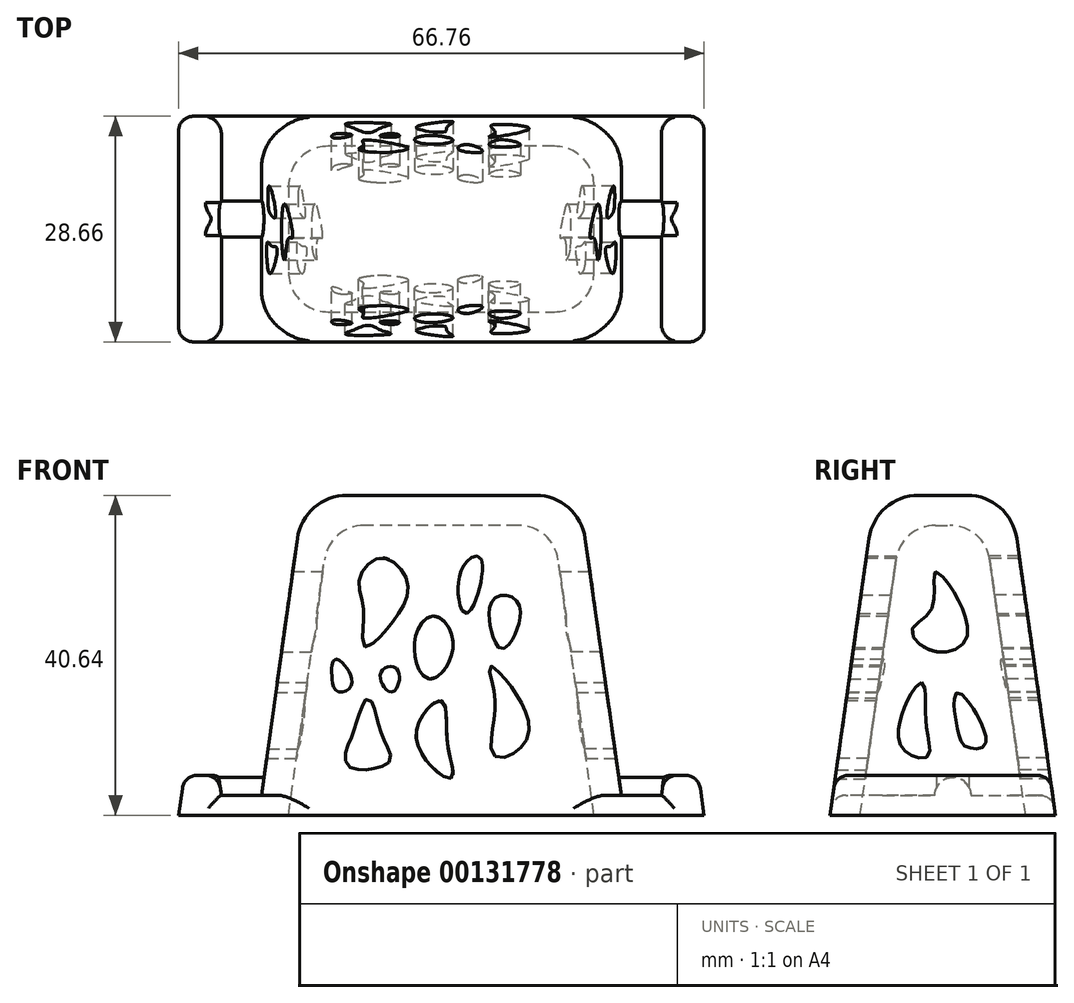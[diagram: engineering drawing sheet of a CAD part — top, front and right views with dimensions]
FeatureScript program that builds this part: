
annotation { "Feature Type Name" : "Feature", "Feature Type Description" : "" }
export const myFeature = defineFeature(function(context is Context, id is Id, definition is map)
    precondition{}
    {
        {
            var Q0;
            Q0=qCreatedBy(makeId("Top.planeOp"),FACE);
            cPlane(context, id + "F0", {"entities" : qUnion([Q0]), "cplaneType" : CPlaneType.OFFSET, "offset" : 38.1 * mm, "oppositeDirection" : true, "width" : 152.4 * mm, "height" : 152.4 * mm});
        }
        {
            var Q0;
            Q0=qCreatedBy(id+"F0.planeOp",FACE);
            var sketch = newSketch(context, id + "F1", { "sketchPlane" : qUnion([Q0])});
            skLineSegment(sketch, "E0.bottom", {"start": v(22.86, -13.97) * mm, "end": v(-22.86, -13.97) * mm});
            skLineSegment(sketch, "E0.top", {"start": v(22.86, 13.97) * mm, "end": v(-22.86, 13.97) * mm});
            skLineSegment(sketch, "E0.left", {"start": v(22.86, -13.97) * mm, "end": v(22.86, 13.97) * mm});
            skLineSegment(sketch, "E0.right", {"start": v(-22.86, -13.97) * mm, "end": v(-22.86, 13.97) * mm});
            skPoint(sketch, "E0.middle", {"position": v(0, 0) * mm});
            skLineSegment(sketch, "E1", {"start": v(22.86, 13.97) * mm, "end": v(33.02, 13.97) * mm});
            skLineSegment(sketch, "E2", {"start": v(33.02, 13.97) * mm, "end": v(33.02, -13.97) * mm});
            skLineSegment(sketch, "E3", {"start": v(33.02, -13.97) * mm, "end": v(22.86, -13.97) * mm});
            skLineSegment(sketch, "E4", {"start": v(0, -33.3) * mm, "end": v(0, 38) * mm, "construction": true});
            skPoint(sketch, "E4.endSnap0", {"position": v(0, 13.97) * mm});
            skLineSegment(sketch, "E5.MirrorCS", {"start": v(-33.02, -13.97) * mm, "end": v(-22.86, -13.97) * mm});
            skLineSegment(sketch, "E6.MirrorCS", {"start": v(-22.86, 13.97) * mm, "end": v(-33.02, 13.97) * mm});
            skLineSegment(sketch, "E7.MirrorCS", {"start": v(-33.02, 13.97) * mm, "end": v(-33.02, -13.97) * mm});
            skLineSegment(sketch, "E8", {"start": v(27.94, 13.97) * mm, "end": v(27.94, -13.97) * mm});
            skLineSegment(sketch, "E9.MirrorCS", {"start": v(-27.94, 13.97) * mm, "end": v(-27.94, -13.97) * mm});
            skLineSegment(sketch, "E10", {"start": v(25.4, 13.97) * mm, "end": v(25.4, -13.97) * mm, "construction": true});
            skLineSegment(sketch, "E11.MirrorCS", {"start": v(-25.4, 13.97) * mm, "end": v(-25.4, -13.97) * mm, "construction": true});
            skLineSegment(sketch, "E12", {"start": v(27.94, 1.27) * mm, "end": v(22.86, 1.27) * mm, "construction": true});
            skLineSegment(sketch, "E13", {"start": v(30.12, 3.56) * mm, "end": v(-3.65, 3.56) * mm});
            skLineSegment(sketch, "E14", {"start": v(-3.65, 3.56) * mm, "end": v(-30.88, 3.56) * mm});
            skLineSegment(sketch, "E15", {"start": v(-30.88, 3.56) * mm, "end": v(-30.88, 1.27) * mm});
            skLineSegment(sketch, "E16", {"start": v(30.12, 3.56) * mm, "end": v(30.12, 1.27) * mm});
            skLineSegment(sketch, "E17", {"start": v(-30.88, 1.27) * mm, "end": v(30.12, 1.27) * mm});
            skSolve(sketch);
        }
        {
            var Q0;
            Q0=makeQuery(id+"F1.imprint","IMPRINT",FACE,{"disambiguationData":[TD([[makeQuery(id+"F1.imprint","IMPRINT",EDGE,{"derivedFrom":sQuery(id+"F1.wireOp",EDGE,"E0.bottom")}),-1.0]])]});
            var Q1;
            {var subQ6=sQuery(id+"F1.wireOp",EDGE,"E0.top");Q1=makeQuery(id+"F1.imprint","IMPRINT",FACE,{"disambiguationData":[TD([[makeQuery(id+"F1.imprint","IMPRINT",EDGE,{"derivedFrom":subQ6}),1.0]])]});}
            var Q2;
            {var subQ3=sQuery(id+"F1.wireOp",EDGE,"E0.left");var subQ5=sQuery(id+"F1.wireOp",EDGE,"E17");var subQ6=makeQuery(id+"F1.imprint","INTERSECT",VERTEX,{"derivedFrom":[subQ3,subQ5]});Q2=makeQuery(id+"F1.imprint","IMPRINT",FACE,{"disambiguationData":[TD([[makeQuery(id+"F1.imprint","IMPRINT",EDGE,{"disambiguationData":[TD([[subQ6,-1.0]])],"derivedFrom":subQ3}),1.0]])]});}
            var Q3;
            Q3=sQuery(id+"F1.wireOp",EDGE,"E0.right");
            var Q4;
            Q4=sQuery(id+"F1.wireOp",EDGE,"E0.top");
            var Q5;
            Q5=sQuery(id+"F1.wireOp",EDGE,"E0.left");
            var Q6;
            Q6=sQuery(id+"F1.wireOp",EDGE,"E0.bottom");
            var Q7;
            Q7=qCreatedBy(makeId("Top.planeOp"),FACE);
            extrude(context, id + "F2", {"entities" : qUnion([Q0, Q1, Q2]), "surfaceEntities" : qUnion([Q3, Q4, Q5, Q6]), "endBound" : BoundingType.UP_TO_SURFACE, "endBoundEntityFace" : qUnion([Q7]), "depth" : 25.4 * mm, "hasDraft" : true, "draftAngle" : 8 * degree, "draftPullDirection" : true});
        }
        {
            var Q0;
            {var subQ0=sQuery(id+"F1.wireOp",EDGE,"E7.MirrorCS");Q0=makeQuery(id+"F1.imprint","IMPRINT",FACE,{"disambiguationData":[TD([[makeQuery(id+"F1.imprint","IMPRINT",EDGE,{"derivedFrom":subQ0}),1.0]])]});}
            var Q1;
            {var subQ0=sQuery(id+"F1.wireOp",EDGE,"E0.right");Q1=makeQuery(id+"F1.imprint","IMPRINT",FACE,{"disambiguationData":[TD([[makeQuery(id+"F1.imprint","IMPRINT",EDGE,{"derivedFrom":subQ0}),1.0]])]});}
            var Q2;
            Q2=makeQuery(id+"F1.imprint","IMPRINT",FACE,{"disambiguationData":[TD([[makeQuery(id+"F1.imprint","IMPRINT",EDGE,{"derivedFrom":sQuery(id+"F1.wireOp",EDGE,"E0.bottom")}),-1.0]])]});
            var Q3;
            {var subQ0=sQuery(id+"F1.wireOp",EDGE,"E0.left");Q3=makeQuery(id+"F1.imprint","IMPRINT",FACE,{"disambiguationData":[TD([[makeQuery(id+"F1.imprint","IMPRINT",EDGE,{"derivedFrom":subQ0}),-1.0]])]});}
            var Q4;
            {var subQ0=sQuery(id+"F1.wireOp",EDGE,"E2");Q4=makeQuery(id+"F1.imprint","IMPRINT",FACE,{"disambiguationData":[TD([[makeQuery(id+"F1.imprint","IMPRINT",EDGE,{"derivedFrom":subQ0}),-1.0]])]});}
            var Q5;
            {var subQ6=sQuery(id+"F1.wireOp",EDGE,"E0.top");Q5=makeQuery(id+"F1.imprint","IMPRINT",FACE,{"disambiguationData":[TD([[makeQuery(id+"F1.imprint","IMPRINT",EDGE,{"derivedFrom":subQ6}),1.0]])]});}
            var Q6;
            {var subQ3=sQuery(id+"F1.wireOp",EDGE,"E0.left");var subQ5=sQuery(id+"F1.wireOp",EDGE,"E17");var subQ6=makeQuery(id+"F1.imprint","INTERSECT",VERTEX,{"derivedFrom":[subQ3,subQ5]});Q6=makeQuery(id+"F1.imprint","IMPRINT",FACE,{"disambiguationData":[TD([[makeQuery(id+"F1.imprint","IMPRINT",EDGE,{"disambiguationData":[TD([[subQ6,-1.0]])],"derivedFrom":subQ3}),1.0]])]});}
            var Q7;
            {var subQ5=sQuery(id+"F1.wireOp",EDGE,"E15");Q7=makeQuery(id+"F1.imprint","IMPRINT",FACE,{"disambiguationData":[TD([[makeQuery(id+"F1.imprint","IMPRINT",EDGE,{"derivedFrom":subQ5}),1.0]])]});}
            var Q8;
            {var subQ5=sQuery(id+"F1.wireOp",EDGE,"E16");Q8=makeQuery(id+"F1.imprint","IMPRINT",FACE,{"disambiguationData":[TD([[makeQuery(id+"F1.imprint","IMPRINT",EDGE,{"derivedFrom":subQ5}),-1.0]])]});}
            extrude(context, id + "F3", {"entities" : qUnion([Q0, Q1, Q2, Q3, Q4, Q5, Q6, Q7, Q8]), "operationType" : NewBodyOperationType.ADD, "oppositeDirection" : true, "depth" : 2.54 * mm, "hasDraft" : true, "draftAngle" : 8 * degree});
        }
        {
            var Q0;
            {var subQ1=sQuery(id+"F1.wireOp",EDGE,"E2");Q0=makeQuery(id+"F1.imprint","IMPRINT",FACE,{"disambiguationData":[TD([[makeQuery(id+"F1.imprint","IMPRINT",EDGE,{"derivedFrom":subQ1}),-1.0]])]});}
            var Q1;
            {var subQ4=sQuery(id+"F1.wireOp",EDGE,"E7.MirrorCS");Q1=makeQuery(id+"F1.imprint","IMPRINT",FACE,{"disambiguationData":[TD([[makeQuery(id+"F1.imprint","IMPRINT",EDGE,{"derivedFrom":subQ4}),1.0]])]});}
            var Q2;
            {var subQ5=sQuery(id+"F1.wireOp",EDGE,"E16");Q2=makeQuery(id+"F1.imprint","IMPRINT",FACE,{"disambiguationData":[TD([[makeQuery(id+"F1.imprint","IMPRINT",EDGE,{"derivedFrom":subQ5}),-1.0]])]});}
            var Q3;
            {var subQ5=sQuery(id+"F1.wireOp",EDGE,"E15");Q3=makeQuery(id+"F1.imprint","IMPRINT",FACE,{"disambiguationData":[TD([[makeQuery(id+"F1.imprint","IMPRINT",EDGE,{"derivedFrom":subQ5}),1.0]])]});}
            extrude(context, id + "F4", {"entities" : qUnion([Q0, Q1, Q2, Q3]), "operationType" : NewBodyOperationType.ADD, "depth" : 2.54 * mm, "hasDraft" : true, "draftAngle" : 8 * degree, "draftPullDirection" : true});
        }
        {
            var Q0;
            {var subQ0=sQuery(id+"F1.wireOp",EDGE,"E17");var subQ1=sQuery(id+"F1.wireOp",EDGE,"E0.right");var subQ2=makeQuery(id+"F1.imprint","INTERSECT",VERTEX,{"derivedFrom":[subQ1,subQ0]});Q0=makeQuery(id+"F1.imprint","IMPRINT",FACE,{"disambiguationData":[TD([[makeQuery(id+"F1.imprint","IMPRINT",EDGE,{"disambiguationData":[TD([[subQ2,-1.0]])],"derivedFrom":subQ1}),1.0]])]});}
            var Q1;
            {var subQ0=sQuery(id+"F1.wireOp",EDGE,"E17");var subQ1=sQuery(id+"F1.wireOp",EDGE,"E0.left");var subQ2=makeQuery(id+"F1.imprint","INTERSECT",VERTEX,{"derivedFrom":[subQ1,subQ0]});Q1=makeQuery(id+"F1.imprint","IMPRINT",FACE,{"disambiguationData":[TD([[makeQuery(id+"F1.imprint","IMPRINT",EDGE,{"disambiguationData":[TD([[subQ2,-1.0]])],"derivedFrom":subQ1}),-1.0]])]});}
            var Q2;
            {var subQ5=sQuery(id+"F1.wireOp",EDGE,"E16");Q2=makeQuery(id+"F1.imprint","IMPRINT",FACE,{"disambiguationData":[TD([[makeQuery(id+"F1.imprint","IMPRINT",EDGE,{"derivedFrom":subQ5}),-1.0]])]});}
            var Q3;
            {var subQ5=sQuery(id+"F1.wireOp",EDGE,"E15");Q3=makeQuery(id+"F1.imprint","IMPRINT",FACE,{"disambiguationData":[TD([[makeQuery(id+"F1.imprint","IMPRINT",EDGE,{"derivedFrom":subQ5}),1.0]])]});}
            var Q4;
            {var subQ3=sQuery(id+"F1.wireOp",EDGE,"E0.left");var subQ5=sQuery(id+"F1.wireOp",EDGE,"E17");var subQ6=makeQuery(id+"F1.imprint","INTERSECT",VERTEX,{"derivedFrom":[subQ3,subQ5]});Q4=makeQuery(id+"F1.imprint","IMPRINT",FACE,{"disambiguationData":[TD([[makeQuery(id+"F1.imprint","IMPRINT",EDGE,{"disambiguationData":[TD([[subQ6,-1.0]])],"derivedFrom":subQ3}),1.0]])]});}
            var Q5;
            Q5=sQuery(id+"F1.wireOp",EDGE,"E17");
            revolve(context, id + "F5", {"operationType" : NewBodyOperationType.ADD, "entities" : qUnion([Q0, Q1, Q2, Q3, Q4]), "axis" : qUnion([Q5]), "revolveType" : RevolveType.FULL});
        }
        {
            var Q0;
            Q0=makeQuery(id+"F2.opExtrude","CAP_FACE",FACE,{"disambiguationData":[OSD([sQuery(id+"F1.wireOp",EDGE,"E0.bottom"),sQuery(id+"F1.wireOp",EDGE,"E0.top"),sQuery(id+"F1.wireOp",EDGE,"E0.left"),sQuery(id+"F1.wireOp",EDGE,"E0.right")])],"isStart":false});
            var sketch = newSketch(context, id + "F6", { "sketchPlane" : qUnion([Q0])});
            skLineSegment(sketch, "E18.0", {"start": v(-13.7, -4.8) * mm, "end": v(13.7, -4.8) * mm});
            skLineSegment(sketch, "E18.1", {"start": v(-13.7, 4.8) * mm, "end": v(-13.7, -4.8) * mm});
            skLineSegment(sketch, "E18.2", {"start": v(13.7, 4.8) * mm, "end": v(-13.7, 4.8) * mm});
            skLineSegment(sketch, "E18.3", {"start": v(13.7, -4.8) * mm, "end": v(13.7, 4.8) * mm});
            skSolve(sketch);
        }
        {
            var Q0;
            Q0 = qSketchRegion(id + "F6", true);
            extrude(context, id + "F7", {"entities" : qUnion([Q0]), "operationType" : NewBodyOperationType.REMOVE, "endBound" : BoundingType.THROUGH_ALL, "oppositeDirection" : true, "depth" : 25.4 * mm, "hasDraft" : true, "draftAngle" : 8 * degree});
        }
        {
            var Q0;
            Q0=makeQuery(id+"F2.opExtrude","CAP_FACE",FACE,{"disambiguationData":[OSD([sQuery(id+"F1.wireOp",EDGE,"E0.bottom"),sQuery(id+"F1.wireOp",EDGE,"E0.top"),sQuery(id+"F1.wireOp",EDGE,"E0.left"),sQuery(id+"F1.wireOp",EDGE,"E0.right")])],"isStart":false});
            var sketch = newSketch(context, id + "F8", { "sketchPlane" : qUnion([Q0])});
            skLineSegment(sketch, "E19.0", {"start": v(17.5, 8.62) * mm, "end": v(-17.5, 8.62) * mm});
            skLineSegment(sketch, "E20.0", {"start": v(-17.5, -8.62) * mm, "end": v(-17.5, 8.62) * mm});
            skLineSegment(sketch, "E21.0", {"start": v(17.5, -8.62) * mm, "end": v(17.5, 8.62) * mm});
            skLineSegment(sketch, "E22.0", {"start": v(17.5, -8.62) * mm, "end": v(-17.5, -8.62) * mm});
            skSolve(sketch);
        }
        {
            var Q0;
            Q0 = qSketchRegion(id + "F8", true);
            extrude(context, id + "F9", {"entities" : qUnion([Q0]), "operationType" : NewBodyOperationType.ADD, "oppositeDirection" : true, "depth" : 3.8 * mm});
        }
        {
            var Q0;
            Q0=makeQuery(id+"F9.boolean.opBoolean","INTERSECT",EDGE,{"derivedFrom":[makeQuery(id+"F7.boolean.opBoolean","COPY",FACE,{"derivedFrom":makeQuery(id+"F7.opExtrude","SWEPT_FACE",FACE,{"disambiguationData":[OSD([sQuery(id+"F6.wireOp",EDGE,"E18.1")])]})}),makeQuery(id+"F9.opExtrude","CAP_FACE",FACE,{"disambiguationData":[OSD([sQuery(id+"F8.wireOp",EDGE,"E19.0"),sQuery(id+"F8.wireOp",EDGE,"E20.0"),sQuery(id+"F8.wireOp",EDGE,"E21.0"),sQuery(id+"F8.wireOp",EDGE,"E22.0")])],"isStart":false})]});
            var Q1;
            Q1=makeQuery(id+"F9.boolean.opBoolean","INTERSECT",EDGE,{"derivedFrom":[makeQuery(id+"F7.boolean.opBoolean","COPY",FACE,{"derivedFrom":makeQuery(id+"F7.opExtrude","SWEPT_FACE",FACE,{"disambiguationData":[OSD([sQuery(id+"F6.wireOp",EDGE,"E18.0")])]})}),makeQuery(id+"F9.opExtrude","CAP_FACE",FACE,{"disambiguationData":[OSD([sQuery(id+"F8.wireOp",EDGE,"E19.0"),sQuery(id+"F8.wireOp",EDGE,"E20.0"),sQuery(id+"F8.wireOp",EDGE,"E21.0"),sQuery(id+"F8.wireOp",EDGE,"E22.0")])],"isStart":false})]});
            var Q2;
            Q2=makeQuery(id+"F9.boolean.opBoolean","INTERSECT",EDGE,{"derivedFrom":[makeQuery(id+"F7.boolean.opBoolean","COPY",FACE,{"derivedFrom":makeQuery(id+"F7.opExtrude","SWEPT_FACE",FACE,{"disambiguationData":[OSD([sQuery(id+"F6.wireOp",EDGE,"E18.3")])]})}),makeQuery(id+"F9.opExtrude","CAP_FACE",FACE,{"disambiguationData":[OSD([sQuery(id+"F8.wireOp",EDGE,"E19.0"),sQuery(id+"F8.wireOp",EDGE,"E20.0"),sQuery(id+"F8.wireOp",EDGE,"E21.0"),sQuery(id+"F8.wireOp",EDGE,"E22.0")])],"isStart":false})]});
            var Q3;
            Q3=makeQuery(id+"F9.boolean.opBoolean","INTERSECT",EDGE,{"derivedFrom":[makeQuery(id+"F7.boolean.opBoolean","COPY",FACE,{"derivedFrom":makeQuery(id+"F7.opExtrude","SWEPT_FACE",FACE,{"disambiguationData":[OSD([sQuery(id+"F6.wireOp",EDGE,"E18.2")])]})}),makeQuery(id+"F9.opExtrude","CAP_FACE",FACE,{"disambiguationData":[OSD([sQuery(id+"F8.wireOp",EDGE,"E19.0"),sQuery(id+"F8.wireOp",EDGE,"E20.0"),sQuery(id+"F8.wireOp",EDGE,"E21.0"),sQuery(id+"F8.wireOp",EDGE,"E22.0")])],"isStart":false})]});
            fillet(context, id + "F10", {"entities" : qUnion([Q0, Q1, Q2, Q3]), "radius" : 5.08 * mm, "tangentPropagation" : true, "allowEdgeOverflow" : false});
        }
        {
            var Q0;
            Q0=makeQuery(id+"F7.boolean.opBoolean","COPY",EDGE,{"derivedFrom":makeQuery(id+"F7.opExtrude","SWEPT_EDGE",EDGE,{"disambiguationData":[OSD([sQuery(id+"F6.wireOp",EDGE,"E18.0"),sQuery(id+"F6.wireOp",EDGE,"E18.1")])]})});
            var Q1;
            Q1=makeQuery(id+"F7.boolean.opBoolean","COPY",EDGE,{"derivedFrom":makeQuery(id+"F7.opExtrude","SWEPT_EDGE",EDGE,{"disambiguationData":[OSD([sQuery(id+"F6.wireOp",EDGE,"E18.0"),sQuery(id+"F6.wireOp",EDGE,"E18.3")])]})});
            var Q2;
            Q2=makeQuery(id+"F7.boolean.opBoolean","COPY",EDGE,{"derivedFrom":makeQuery(id+"F7.opExtrude","SWEPT_EDGE",EDGE,{"disambiguationData":[OSD([sQuery(id+"F6.wireOp",EDGE,"E18.2"),sQuery(id+"F6.wireOp",EDGE,"E18.3")])]})});
            var Q3;
            Q3=makeQuery(id+"F7.boolean.opBoolean","COPY",EDGE,{"derivedFrom":makeQuery(id+"F7.opExtrude","SWEPT_EDGE",EDGE,{"disambiguationData":[OSD([sQuery(id+"F6.wireOp",EDGE,"E18.1"),sQuery(id+"F6.wireOp",EDGE,"E18.2")])]})});
            fillet(context, id + "F11", {"entities" : qUnion([Q0, Q1, Q2, Q3]), "radius" : 5.08 * mm, "tangentPropagation" : true, "allowEdgeOverflow" : false});
        }
        {
            var Q0;
            Q0=makeQuery(id+"F2.opExtrude","SWEPT_EDGE",EDGE,{"disambiguationData":[OSD([sQuery(id+"F1.wireOp",EDGE,"E0.top"),sQuery(id+"F1.wireOp",EDGE,"E0.right"),sQuery(id+"F1.wireOp",EDGE,"E6.MirrorCS")])]});
            var Q1;
            Q1=makeQuery(id+"F2.opExtrude","SWEPT_EDGE",EDGE,{"disambiguationData":[OSD([sQuery(id+"F1.wireOp",EDGE,"E0.bottom"),sQuery(id+"F1.wireOp",EDGE,"E0.right"),sQuery(id+"F1.wireOp",EDGE,"E5.MirrorCS")])]});
            var Q2;
            Q2=makeQuery(id+"F2.opExtrude","SWEPT_EDGE",EDGE,{"disambiguationData":[OSD([sQuery(id+"F1.wireOp",EDGE,"E0.bottom"),sQuery(id+"F1.wireOp",EDGE,"E0.left"),sQuery(id+"F1.wireOp",EDGE,"E3")])]});
            var Q3;
            Q3=makeQuery(id+"F2.opExtrude","SWEPT_EDGE",EDGE,{"disambiguationData":[OSD([sQuery(id+"F1.wireOp",EDGE,"E0.top"),sQuery(id+"F1.wireOp",EDGE,"E0.left"),sQuery(id+"F1.wireOp",EDGE,"E1")])]});
            var Q4;
            Q4=makeQuery(id+"F2.opExtrude","CAP_EDGE",EDGE,{"disambiguationData":[OSD([sQuery(id+"F1.wireOp",EDGE,"E0.top")])],"isStart":false});
            var Q5;
            Q5=makeQuery(id+"F2.opExtrude","CAP_EDGE",EDGE,{"disambiguationData":[OSD([sQuery(id+"F1.wireOp",EDGE,"E0.left")])],"isStart":false});
            var Q6;
            Q6=makeQuery(id+"F2.opExtrude","CAP_EDGE",EDGE,{"disambiguationData":[OSD([sQuery(id+"F1.wireOp",EDGE,"E0.bottom")])],"isStart":false});
            var Q7;
            Q7=makeQuery(id+"F2.opExtrude","CAP_EDGE",EDGE,{"disambiguationData":[OSD([sQuery(id+"F1.wireOp",EDGE,"E0.right")])],"isStart":false});
            fillet(context, id + "F12", {"entities" : qUnion([Q0, Q1, Q2, Q3, Q4, Q5, Q6, Q7]), "radius" : 6.35 * mm, "tangentPropagation" : true, "allowEdgeOverflow" : false});
        }
        {
            var Q0;
            Q0=qCreatedBy(makeId("Front.planeOp"),FACE);
            var sketch = newSketch(context, id + "F13", { "sketchPlane" : qUnion([Q0])});
            skFitSpline(sketch, "E23", {"points": [v(-6.63, -33.93) * mm, v(-11.75, -34.44) * mm, v(-11.92, -31.92) * mm, v(-11.16, -30.07) * mm, v(-9.31, -25.7) * mm, v(-7.38, -30.83) * mm, v(-6.63, -33.93) * mm]});
            skFitSpline(sketch, "E24", {"points": [v(-9.68, -19.27) * mm, v(-5.29, -14.74) * mm, v(-4.42, -10.67) * mm, v(-7.55, -7.94) * mm, v(-10.4, -10.46) * mm, v(-9.9, -14.55) * mm, v(-9.68, -19.27) * mm]});
            skFitSpline(sketch, "E25", {"points": [v(6.8, -33.18) * mm, v(6.8, -25.96) * mm, v(6.15, -21.58) * mm, v(11.13, -30.04) * mm, v(6.8, -33.18) * mm]});
            skFitSpline(sketch, "E26", {"points": [v(1.24, -35.99) * mm, v(-3.19, -30.74) * mm, v(0, -26.08) * mm, v(0.76, -31.33) * mm, v(1.24, -35.99) * mm]});
            skFitSpline(sketch, "E27", {"points": [v(3.25, -15) * mm, v(2.5, -9.62) * mm, v(5.01, -8.03) * mm, v(3.25, -15) * mm]});
            skFitSpline(sketch, "E28", {"points": [v(6.36, -17.26) * mm, v(6.86, -12.98) * mm, v(9.88, -13.9) * mm, v(7.95, -19.45) * mm, v(6.36, -17.26) * mm]});
            skFitSpline(sketch, "E29", {"points": [v(-1.53, -23.3) * mm, v(1.49, -19.28) * mm, v(-0.86, -15.33) * mm, v(-3.38, -18.52) * mm, v(-1.53, -23.3) * mm]});
            skFitSpline(sketch, "E30", {"points": [v(-6.32, -24.99) * mm, v(-7.76, -22.8) * mm, v(-6.32, -21.71) * mm, v(-5.31, -22.89) * mm, v(-6.32, -24.99) * mm]});
            skFitSpline(sketch, "E31", {"points": [v(-13.04, -24.99) * mm, v(-13.88, -23.3) * mm, v(-13.37, -20.8) * mm, v(-11.36, -23.9) * mm, v(-13.04, -24.99) * mm]});
            skSolve(sketch);
        }
        {
            var Q0;
            Q0 = qSketchRegion(id + "F13", true);
            extrude(context, id + "F14", {"entities" : qUnion([Q0]), "operationType" : NewBodyOperationType.REMOVE, "endBound" : BoundingType.SYMMETRIC, "oppositeDirection" : true, "depth" : 52 * mm});
        }
        {
            var Q0;
            Q0=qCreatedBy(makeId("Right.planeOp"),FACE);
            var sketch = newSketch(context, id + "F15", { "sketchPlane" : qUnion([Q0])});
            skFitSpline(sketch, "E32", {"points": [v(-0.94, -9.68) * mm, v(-1.33, -14.18) * mm, v(-3.93, -17.07) * mm, v(-1.24, -19.77) * mm, v(3.16, -17.47) * mm, v(-0.94, -9.68) * mm]});
            skFitSpline(sketch, "E33", {"points": [v(-2.73, -23.76) * mm, v(-5.53, -31.25) * mm, v(-2.03, -33.25) * mm, v(-2.13, -29.05) * mm, v(-2.73, -23.76) * mm]});
            skFitSpline(sketch, "E34", {"points": [v(2.06, -30.45) * mm, v(3.26, -32.05) * mm, v(5.45, -31.45) * mm, v(1.86, -25.06) * mm, v(2.06, -30.45) * mm]});
            skSolve(sketch);
        }
        {
            var Q0;
            Q0 = qSketchRegion(id + "F15", true);
            extrude(context, id + "F16", {"entities" : qUnion([Q0]), "operationType" : NewBodyOperationType.REMOVE, "endBound" : BoundingType.SYMMETRIC, "oppositeDirection" : true, "depth" : 86.62 * mm});
        }
        {
            var Q0;
            Q0=makeQuery(id+"F4.opExtrude","CAP_EDGE",EDGE,{"disambiguationData":[OSD([sQuery(id+"F1.wireOp",EDGE,"E7.MirrorCS")])],"isStart":false});
            var Q1;
            Q1=makeQuery(id+"F4.opExtrude","CAP_EDGE",EDGE,{"disambiguationData":[OSD([sQuery(id+"F1.wireOp",EDGE,"E9.MirrorCS")])],"isStart":false});
            var Q2;
            {var subQ0=sQuery(id+"F1.wireOp",EDGE,"E7.MirrorCS");var subQ1=sQuery(id+"F1.wireOp",EDGE,"E5.MirrorCS");Q2=makeQuery(id+"F4.boolean.opBoolean","MERGE",EDGE,{"derivedFrom":[makeQuery(id+"F3.opExtrude","SWEPT_EDGE",EDGE,{"disambiguationData":[OSD([subQ1,subQ0])]}),makeQuery(id+"F4.opExtrude","SWEPT_EDGE",EDGE,{"disambiguationData":[OSD([subQ1,subQ0])]})]});}
            var Q3;
            {var subQ0=sQuery(id+"F1.wireOp",EDGE,"E7.MirrorCS");var subQ1=sQuery(id+"F1.wireOp",EDGE,"E6.MirrorCS");Q3=makeQuery(id+"F4.boolean.opBoolean","MERGE",EDGE,{"derivedFrom":[makeQuery(id+"F3.opExtrude","SWEPT_EDGE",EDGE,{"disambiguationData":[OSD([subQ1,subQ0])]}),makeQuery(id+"F4.opExtrude","SWEPT_EDGE",EDGE,{"disambiguationData":[OSD([subQ1,subQ0])]})]});}
            var Q4;
            {var subQ0=sQuery(id+"F1.wireOp",EDGE,"E6.MirrorCS");var subQ1=sQuery(id+"F1.wireOp",EDGE,"E1");var subQ2=sQuery(id+"F1.wireOp",EDGE,"E0.top");Q4=makeQuery(id+"F3.boolean.opBoolean","SPLIT",EDGE,{"disambiguationData":[TD([makeQuery(id+"F2.opExtrude","SWEPT_FACE",FACE,{"disambiguationData":[OSD([sQuery(id+"F1.wireOp",EDGE,"E0.left")])]})])],"derivedFrom":makeQuery(id+"F3.opExtrude","CAP_EDGE",EDGE,{"disambiguationData":[OSD([subQ2,subQ1,subQ0])],"isStart":true})});}
            var Q5;
            {var subQ0=sQuery(id+"F1.wireOp",EDGE,"E6.MirrorCS");var subQ1=sQuery(id+"F1.wireOp",EDGE,"E1");var subQ2=sQuery(id+"F1.wireOp",EDGE,"E0.top");Q5=makeQuery(id+"F3.boolean.opBoolean","SPLIT",EDGE,{"disambiguationData":[TD([makeQuery(id+"F2.opExtrude","SWEPT_FACE",FACE,{"disambiguationData":[OSD([sQuery(id+"F1.wireOp",EDGE,"E0.right")])]})])],"derivedFrom":makeQuery(id+"F3.opExtrude","CAP_EDGE",EDGE,{"disambiguationData":[OSD([subQ2,subQ1,subQ0])],"isStart":true})});}
            var Q6;
            {var subQ0=sQuery(id+"F1.wireOp",EDGE,"E5.MirrorCS");var subQ1=sQuery(id+"F1.wireOp",EDGE,"E3");var subQ2=sQuery(id+"F1.wireOp",EDGE,"E0.bottom");Q6=makeQuery(id+"F3.boolean.opBoolean","SPLIT",EDGE,{"disambiguationData":[TD([makeQuery(id+"F2.opExtrude","SWEPT_FACE",FACE,{"disambiguationData":[OSD([sQuery(id+"F1.wireOp",EDGE,"E0.right")])]})])],"derivedFrom":makeQuery(id+"F3.opExtrude","CAP_EDGE",EDGE,{"disambiguationData":[OSD([subQ2,subQ1,subQ0])],"isStart":true})});}
            var Q7;
            {var subQ0=sQuery(id+"F1.wireOp",EDGE,"E5.MirrorCS");var subQ1=sQuery(id+"F1.wireOp",EDGE,"E3");var subQ2=sQuery(id+"F1.wireOp",EDGE,"E0.bottom");Q7=makeQuery(id+"F3.boolean.opBoolean","SPLIT",EDGE,{"disambiguationData":[TD([makeQuery(id+"F2.opExtrude","SWEPT_FACE",FACE,{"disambiguationData":[OSD([sQuery(id+"F1.wireOp",EDGE,"E0.left")])]})])],"derivedFrom":makeQuery(id+"F3.opExtrude","CAP_EDGE",EDGE,{"disambiguationData":[OSD([subQ2,subQ1,subQ0])],"isStart":true})});}
            var Q8;
            Q8=makeQuery(id+"F4.opExtrude","SWEPT_EDGE",EDGE,{"disambiguationData":[OSD([sQuery(id+"F1.wireOp",EDGE,"E5.MirrorCS"),sQuery(id+"F1.wireOp",EDGE,"E9.MirrorCS")])]});
            var Q9;
            Q9=makeQuery(id+"F4.opExtrude","CAP_EDGE",EDGE,{"disambiguationData":[OSD([sQuery(id+"F1.wireOp",EDGE,"E5.MirrorCS")])],"isStart":false});
            var Q10;
            Q10=makeQuery(id+"F4.opExtrude","SWEPT_EDGE",EDGE,{"disambiguationData":[OSD([sQuery(id+"F1.wireOp",EDGE,"E3"),sQuery(id+"F1.wireOp",EDGE,"E8")])]});
            var Q11;
            {var subQ0=sQuery(id+"F1.wireOp",EDGE,"E3");var subQ1=sQuery(id+"F1.wireOp",EDGE,"E2");Q11=makeQuery(id+"F4.boolean.opBoolean","MERGE",EDGE,{"derivedFrom":[makeQuery(id+"F3.opExtrude","SWEPT_EDGE",EDGE,{"disambiguationData":[OSD([subQ1,subQ0])]}),makeQuery(id+"F4.opExtrude","SWEPT_EDGE",EDGE,{"disambiguationData":[OSD([subQ1,subQ0])]})]});}
            var Q12;
            Q12=makeQuery(id+"F4.opExtrude","CAP_EDGE",EDGE,{"disambiguationData":[OSD([sQuery(id+"F1.wireOp",EDGE,"E3")])],"isStart":false});
            var Q13;
            Q13=makeQuery(id+"F4.opExtrude","CAP_EDGE",EDGE,{"disambiguationData":[OSD([sQuery(id+"F1.wireOp",EDGE,"E8")])],"isStart":false});
            var Q14;
            Q14=makeQuery(id+"F4.opExtrude","CAP_EDGE",EDGE,{"disambiguationData":[OSD([sQuery(id+"F1.wireOp",EDGE,"E2")])],"isStart":false});
            var Q15;
            {var subQ0=sQuery(id+"F1.wireOp",EDGE,"E2");var subQ1=sQuery(id+"F1.wireOp",EDGE,"E1");Q15=makeQuery(id+"F4.boolean.opBoolean","MERGE",EDGE,{"derivedFrom":[makeQuery(id+"F3.opExtrude","SWEPT_EDGE",EDGE,{"disambiguationData":[OSD([subQ1,subQ0])]}),makeQuery(id+"F4.opExtrude","SWEPT_EDGE",EDGE,{"disambiguationData":[OSD([subQ1,subQ0])]})]});}
            var Q16;
            Q16=makeQuery(id+"F4.opExtrude","CAP_EDGE",EDGE,{"disambiguationData":[OSD([sQuery(id+"F1.wireOp",EDGE,"E1")])],"isStart":false});
            var Q17;
            Q17=makeQuery(id+"F4.opExtrude","SWEPT_EDGE",EDGE,{"disambiguationData":[OSD([sQuery(id+"F1.wireOp",EDGE,"E1"),sQuery(id+"F1.wireOp",EDGE,"E8")])]});
            var Q18;
            Q18=makeQuery(id+"F4.opExtrude","SWEPT_EDGE",EDGE,{"disambiguationData":[OSD([sQuery(id+"F1.wireOp",EDGE,"E6.MirrorCS"),sQuery(id+"F1.wireOp",EDGE,"E9.MirrorCS")])]});
            var Q19;
            Q19=makeQuery(id+"F4.opExtrude","CAP_EDGE",EDGE,{"disambiguationData":[OSD([sQuery(id+"F1.wireOp",EDGE,"E6.MirrorCS")])],"isStart":false});
            fillet(context, id + "F17", {"entities" : qUnion([Q0, Q1, Q2, Q3, Q4, Q5, Q6, Q7, Q8, Q9, Q10, Q11, Q12, Q13, Q14, Q15, Q16, Q17, Q18, Q19]), "radius" : 1.9 * mm, "tangentPropagation" : true, "allowEdgeOverflow" : false});
        }
    });
